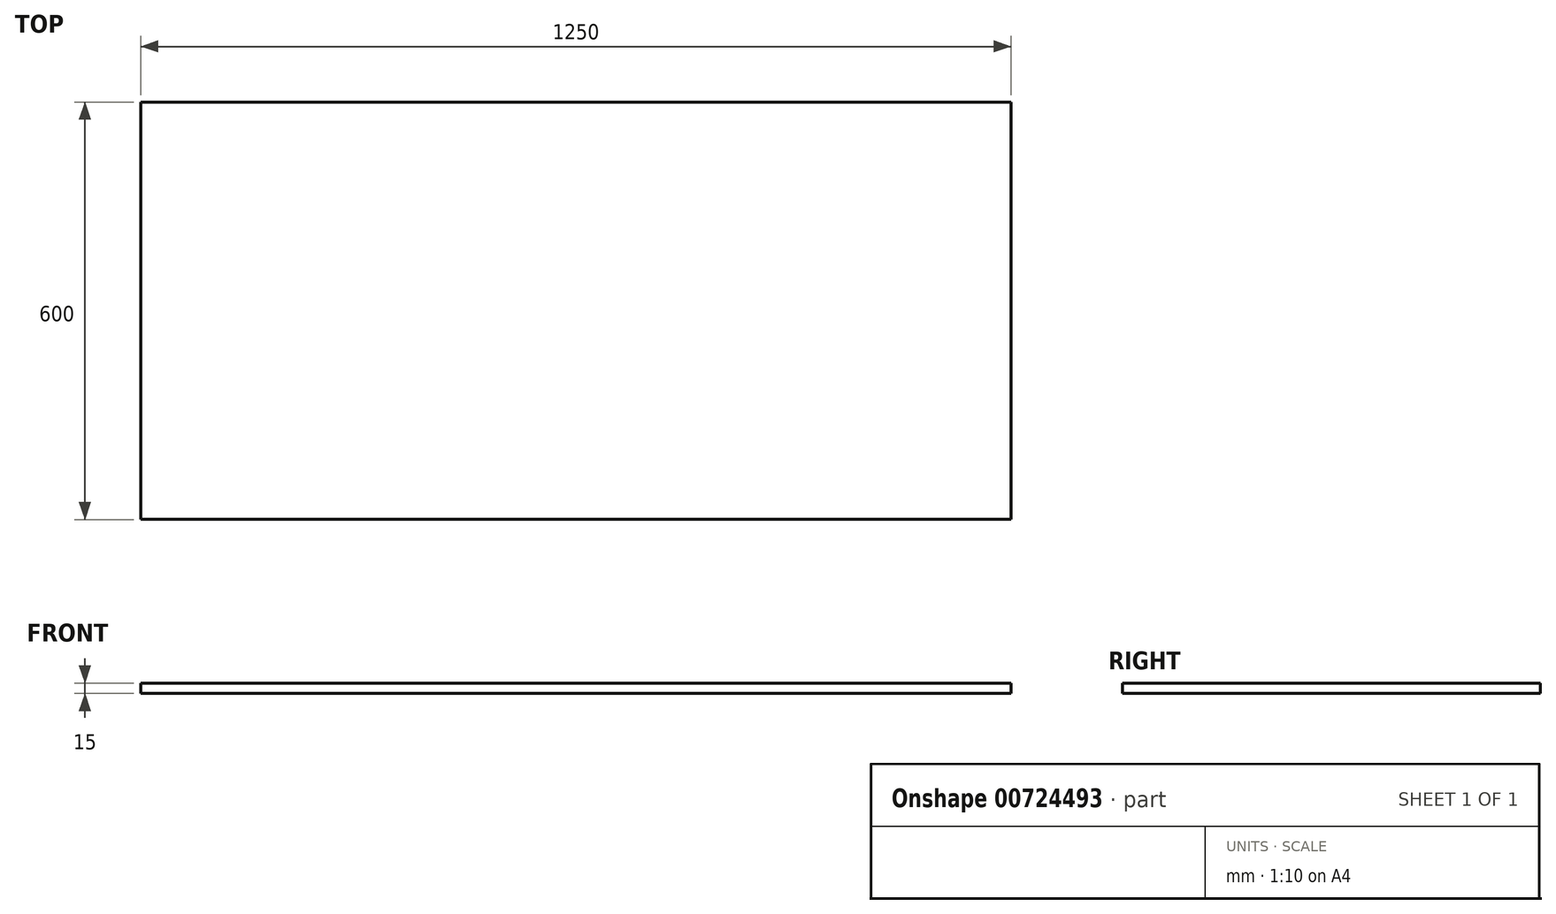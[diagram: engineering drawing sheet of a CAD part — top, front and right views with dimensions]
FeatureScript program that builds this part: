
annotation { "Feature Type Name" : "Feature", "Feature Type Description" : "" }
export const myFeature = defineFeature(function(context is Context, id is Id, definition is map)
    precondition{}
    {
        {
            var Q0;
            Q0=qCreatedBy(makeId("Right.planeOp"),FACE);
            var sketch = newSketch(context, id + "F0", { "sketchPlane" : qUnion([Q0])});
            skLineSegment(sketch, "E0.bottom", {"start": v(-51.27, 13.1) * mm, "end": v(548.73, 13.1) * mm});
            skLineSegment(sketch, "E0.top", {"start": v(-51.27, 28.1) * mm, "end": v(548.73, 28.1) * mm});
            skLineSegment(sketch, "E0.left", {"start": v(-51.27, 13.1) * mm, "end": v(-51.27, 28.1) * mm});
            skLineSegment(sketch, "E0.right", {"start": v(548.73, 13.1) * mm, "end": v(548.73, 28.1) * mm});
            skSolve(sketch);
        }
        {
            var Q0;
            Q0=makeQuery(id+"F0.imprint","IMPRINT",FACE,{"disambiguationData":[TD([[makeQuery(id+"F0.imprint","IMPRINT",EDGE,{"derivedFrom":sQuery(id+"F0.wireOp",EDGE,"E0.bottom")}),1.0]])]});
            extrude(context, id + "F1", {"entities" : qUnion([Q0]), "depth" : 1250 * mm, "offsetDistance" : 25 * mm});
        }
    });
